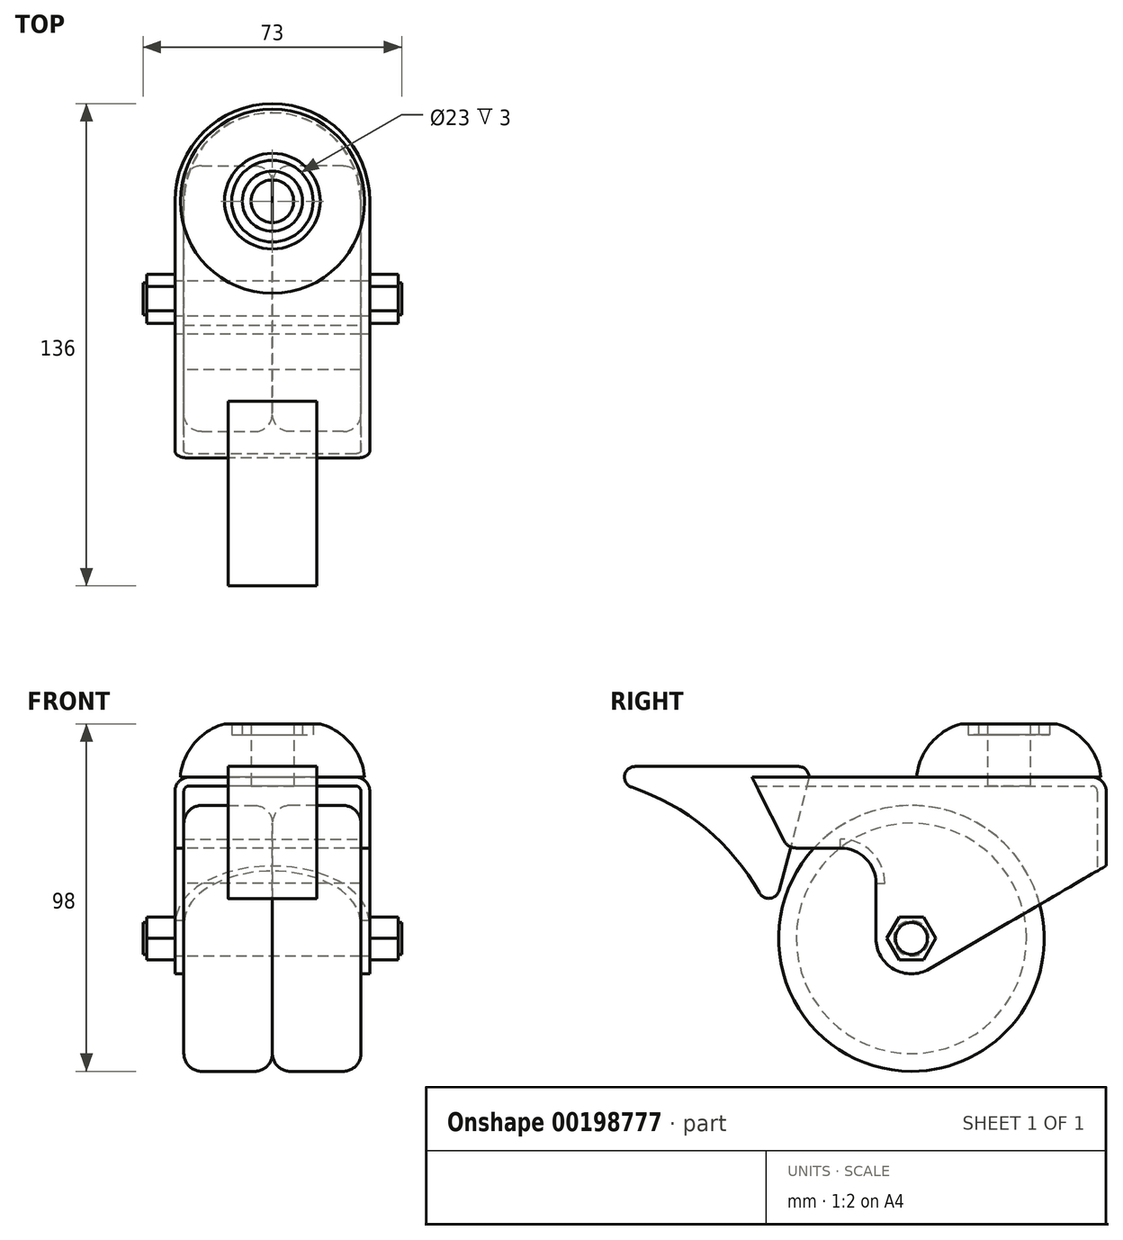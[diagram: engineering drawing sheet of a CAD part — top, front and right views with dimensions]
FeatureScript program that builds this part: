
annotation { "Feature Type Name" : "Feature", "Feature Type Description" : "" }
export const myFeature = defineFeature(function(context is Context, id is Id, definition is map)
    precondition{}
    {
        {
            var Q0;
            Q0=qCreatedBy(makeId("Right.planeOp"),FACE);
            var sketch = newSketch(context, id + "F0", { "sketchPlane" : qUnion([Q0])});
            skCircle(sketch, "E0", {"center": v(0, 0) * mm, "radius": 37.5 * mm});
            skCircle(sketch, "E1", {"center": v(0, 0) * mm, "radius": 5 * mm});
            skSolve(sketch);
        }
        {
            var Q0;
            Q0 = qSketchRegion(id + "F0", true);
            extrude(context, id + "F1", {"entities" : qUnion([Q0]), "depth" : 25 * mm});
        }
        {
            var Q0;
            Q0=makeQuery(id+"F1.opExtrude","CAP_EDGE",EDGE,{"disambiguationData":[OSD([sQuery(id+"F0.wireOp",EDGE,"E0")])],"isStart":true});
            var Q1;
            Q1=makeQuery(id+"F1.opExtrude","CAP_EDGE",EDGE,{"disambiguationData":[OSD([sQuery(id+"F0.wireOp",EDGE,"E0")])],"isStart":false});
            fillet(context, id + "F2", {"entities" : qUnion([Q0, Q1]), "radius" : 5 * mm, "tangentPropagation" : true, "allowEdgeOverflow" : false});
        }
        {
            var Q0;
            Q0=makeQuery(id+"F1.opExtrude","SWEPT_BODY",BODY,{"disambiguationData":[OSD([sQuery(id+"F0.wireOp",EDGE,"E0")])]});
            var Q1;
            Q1=qCreatedBy(makeId("Right.planeOp"),FACE);
            mirror(context, id + "F3", {"operationType" : NewBodyOperationType.ADD, "entities" : qUnion([Q0]), "mirrorPlane" : qUnion([Q1])});
        }
        {
            var Q0;
            Q0=qCreatedBy(makeId("Right.planeOp"),FACE);
            var sketch = newSketch(context, id + "F4", { "sketchPlane" : qUnion([Q0])});
            skCircle(sketch, "E2.0", {"center": v(0, 0) * mm, "radius": 5 * mm});
            skArc(sketch, "E3", {"start": v(-10, 0) * mm, "mid": v(-4.98, -8.67) * mm, "end": v(5.04, -8.64) * mm});
            skLineSegment(sketch, "E4", {"start": v(0, -37.5) * mm, "end": v(0, 45.5) * mm, "construction": true});
            skLineSegment(sketch, "E5", {"start": v(-45, 45.5) * mm, "end": v(55, 45.5) * mm});
            skLineSegment(sketch, "E6", {"start": v(-10, 0) * mm, "end": v(-10, 25.5) * mm});
            skLineSegment(sketch, "E7", {"start": v(-10, 25.5) * mm, "end": v(-35, 25.5) * mm});
            skLineSegment(sketch, "E8", {"start": v(-35, 25.5) * mm, "end": v(-45, 45.5) * mm});
            skLineSegment(sketch, "E9", {"start": v(5.04, -8.64) * mm, "end": v(55, 20.5) * mm});
            skLineSegment(sketch, "E10", {"start": v(55, 20.5) * mm, "end": v(55, 45.5) * mm});
            skSolve(sketch);
        }
        {
            var Q0;
            Q0 = qSketchRegion(id + "F4", true);
            extrude(context, id + "F5", {"entities" : qUnion([Q0]), "depth" : 55 * mm, "symmetric" : true});
        }
        {
            var Q0;
            Q0=makeQuery(id+"F5.opExtrude","CAP_EDGE",EDGE,{"disambiguationData":[OSD([sQuery(id+"F4.wireOp",EDGE,"E10")])],"isStart":false});
            var Q1;
            Q1=makeQuery(id+"F5.opExtrude","CAP_EDGE",EDGE,{"disambiguationData":[OSD([sQuery(id+"F4.wireOp",EDGE,"E10")])],"isStart":true});
            fillet(context, id + "F6", {"entities" : qUnion([Q0, Q1]), "radius" : (55 / 2) * mm, "tangentPropagation" : true, "allowEdgeOverflow" : false});
        }
        {
            var Q0;
            Q0=makeQuery(id+"F5.opExtrude","SWEPT_EDGE",EDGE,{"disambiguationData":[OSD([sQuery(id+"F4.wireOp",EDGE,"E6"),sQuery(id+"F4.wireOp",EDGE,"E7")])]});
            fillet(context, id + "F7", {"entities" : qUnion([Q0]), "radius" : 10 * mm, "tangentPropagation" : true, "allowEdgeOverflow" : false});
        }
        {
            var Q0;
            Q0=makeQuery(id+"F5.opExtrude","CAP_EDGE",EDGE,{"disambiguationData":[OSD([sQuery(id+"F4.wireOp",EDGE,"E5")])],"isStart":false});
            var Q1;
            Q1=makeQuery(id+"F5.opExtrude","SWEPT_EDGE",EDGE,{"disambiguationData":[OSD([sQuery(id+"F4.wireOp",EDGE,"E7"),sQuery(id+"F4.wireOp",EDGE,"E8")])]});
            fillet(context, id + "F8", {"entities" : qUnion([Q0, Q1]), "radius" : 4 * mm, "tangentPropagation" : true, "allowEdgeOverflow" : false});
        }
        {
            var Q0;
            Q0=makeQuery(id+"F5.opExtrude","SWEPT_FACE",FACE,{"disambiguationData":[OSD([sQuery(id+"F4.wireOp",EDGE,"E8")])]});
            var Q1;
            Q1=makeQuery(id+"F8.opFillet","BLEND_FACE",FACE,{"disambiguationData":[OSD([sQuery(id+"F4.wireOp",EDGE,"E7"),sQuery(id+"F4.wireOp",EDGE,"E8")])]});
            var Q2;
            Q2=makeQuery(id+"F5.opExtrude","SWEPT_FACE",FACE,{"disambiguationData":[OSD([sQuery(id+"F4.wireOp",EDGE,"E7")])]});
            var Q3;
            Q3=makeQuery(id+"F5.opExtrude","SWEPT_FACE",FACE,{"disambiguationData":[OSD([sQuery(id+"F4.wireOp",EDGE,"E6")])]});
            var Q4;
            Q4=makeQuery(id+"F5.opExtrude","SWEPT_FACE",FACE,{"disambiguationData":[OSD([sQuery(id+"F4.wireOp",EDGE,"E3")])]});
            var Q5;
            Q5=makeQuery(id+"F5.opExtrude","SWEPT_FACE",FACE,{"disambiguationData":[OSD([sQuery(id+"F4.wireOp",EDGE,"E2.0")])]});
            var Q6;
            Q6=makeQuery(id+"F5.opExtrude","SWEPT_FACE",FACE,{"disambiguationData":[OSD([sQuery(id+"F4.wireOp",EDGE,"E9")])]});
            shell(context, id + "F9", {"entities" : qUnion([Q0, Q1, Q2, Q3, Q4, Q5, Q6]), "thickness" : 2.5 * mm});
        }
        {
            var Q0;
            Q0=qCreatedBy(makeId("Right.planeOp"),FACE);
            var sketch = newSketch(context, id + "F10", { "sketchPlane" : qUnion([Q0])});
            skLineSegment(sketch, "E11.0", {"start": v(27.5, 45.5) * mm, "end": v(51, 45.5) * mm, "construction": true});
            skLineSegment(sketch, "E12", {"start": v(27.5, 45.5) * mm, "end": v(27.5, 60.5) * mm, "construction": true});
            skLineSegment(sketch, "E13.0", {"start": v(33.5, 45.5) * mm, "end": v(33.5, 60.5) * mm});
            skLineSegment(sketch, "E14", {"start": v(33.5, 60.5) * mm, "end": v(36, 60.5) * mm});
            skLineSegment(sketch, "E15", {"start": v(36, 60.5) * mm, "end": v(36, 57.5) * mm});
            skLineSegment(sketch, "E16", {"start": v(36, 57.5) * mm, "end": v(39, 57.5) * mm});
            skLineSegment(sketch, "E17", {"start": v(39, 57.5) * mm, "end": v(39, 60.5) * mm});
            skLineSegment(sketch, "E18", {"start": v(39, 60.5) * mm, "end": v(41, 60.5) * mm});
            skLineSegment(sketch, "E19", {"start": v(33.5, 45.5) * mm, "end": v(53.5, 45.5) * mm});
            skArc(sketch, "E20", {"start": v(53.5, 45.5) * mm, "mid": v(49.62, 54.97) * mm, "end": v(41, 60.5) * mm});
            skSolve(sketch);
        }
        {
            var Q0;
            Q0=makeQuery(id+"F10.imprint","IMPRINT",FACE,{"disambiguationData":[TD([[makeQuery(id+"F10.imprint","IMPRINT",EDGE,{"derivedFrom":sQuery(id+"F10.wireOp",EDGE,"E13.0")}),-1.0]])]});
            var Q1;
            Q1=sQuery(id+"F10.wireOp",EDGE,"E12");
            revolve(context, id + "F11", {"entities" : qUnion([Q0]), "axis" : qUnion([Q1]), "revolveType" : RevolveType.FULL});
        }
        {
            var Q0;
            {var subQ0=sQuery(id+"F4.wireOp",EDGE,"E5");Q0=makeQuery(id+"F9.opShell","OFFSET_FACE",FACE,{"disambiguationData":[OSD([subQ0]),TDD([makeQuery(id+"F5.opExtrude","SWEPT_FACE",FACE,{"disambiguationData":[OSD([subQ0])]})])]});}
            var sketch = newSketch(context, id + "F12", { "sketchPlane" : qUnion([Q0])});
            skCircle(sketch, "E21.0", {"center": v(0, -27.5) * mm, "radius": 6 * mm});
            skSolve(sketch);
        }
        {
            var Q0;
            Q0 = qSketchRegion(id + "F12", true);
            extrude(context, id + "F13", {"entities" : qUnion([Q0]), "operationType" : NewBodyOperationType.REMOVE, "oppositeDirection" : true, "depth" : 43.9 * mm});
        }
        {
            var Q0;
            Q0=makeQuery(id+"F5.opExtrude","CAP_FACE",FACE,{"disambiguationData":[OSD([sQuery(id+"F4.wireOp",EDGE,"E2.0"),sQuery(id+"F4.wireOp",EDGE,"E3"),sQuery(id+"F4.wireOp",EDGE,"E5"),sQuery(id+"F4.wireOp",EDGE,"E6"),sQuery(id+"F4.wireOp",EDGE,"E7"),sQuery(id+"F4.wireOp",EDGE,"E8"),sQuery(id+"F4.wireOp",EDGE,"E9"),sQuery(id+"F4.wireOp",EDGE,"E10")])],"isStart":false});
            var sketch = newSketch(context, id + "F14", { "sketchPlane" : qUnion([Q0])});
            skCircle(sketch, "E22.0", {"center": v(0, 0) * mm, "radius": 5 * mm, "construction": true});
            skCircle(sketch, "E23.cCircle", {"center": v(0, 0) * mm, "radius": 6 * mm, "construction": true});
            skLineSegment(sketch, "E23.0", {"start": v(-3.46, 6) * mm, "end": v(3.46, 6) * mm});
            skLineSegment(sketch, "E23.1", {"start": v(3.46, 6) * mm, "end": v(6.93, 0) * mm});
            skLineSegment(sketch, "E23.2", {"start": v(6.93, 0) * mm, "end": v(3.46, -6) * mm});
            skLineSegment(sketch, "E23.3", {"start": v(3.46, -6) * mm, "end": v(-3.46, -6) * mm});
            skLineSegment(sketch, "E23.4", {"start": v(-3.46, -6) * mm, "end": v(-6.93, 0) * mm});
            skLineSegment(sketch, "E23.5", {"start": v(-6.93, 0) * mm, "end": v(-3.46, 6) * mm});
            skPoint(sketch, "E23.0.midPoint", {"position": v(0, 6) * mm});
            skSolve(sketch);
        }
        {
            var Q0;
            Q0 = qSketchRegion(id + "F14", true);
            extrude(context, id + "F15", {"entities" : qUnion([Q0]), "depth" : 8 * mm});
        }
        {
            var Q0;
            Q0=makeQuery(id+"F15.opExtrude","CAP_FACE",FACE,{"disambiguationData":[OSD([sQuery(id+"F14.wireOp",EDGE,"E23.0"),sQuery(id+"F14.wireOp",EDGE,"E23.1"),sQuery(id+"F14.wireOp",EDGE,"E23.2"),sQuery(id+"F14.wireOp",EDGE,"E23.3"),sQuery(id+"F14.wireOp",EDGE,"E23.4"),sQuery(id+"F14.wireOp",EDGE,"E23.5")])],"isStart":false});
            var sketch = newSketch(context, id + "F16", { "sketchPlane" : qUnion([Q0])});
            skCircle(sketch, "E24", {"center": v(0, 0) * mm, "radius": 4.5 * mm});
            skSolve(sketch);
        }
        {
            var Q0;
            Q0 = qSketchRegion(id + "F16", true);
            extrude(context, id + "F17", {"entities" : qUnion([Q0]), "operationType" : NewBodyOperationType.ADD, "depth" : 1 * mm});
        }
        {
            var Q0;
            Q0=makeQuery(id+"F15.opExtrude","SWEPT_BODY",BODY,{"disambiguationData":[OSD([sQuery(id+"F14.wireOp",EDGE,"E23.0"),sQuery(id+"F14.wireOp",EDGE,"E23.1"),sQuery(id+"F14.wireOp",EDGE,"E23.2"),sQuery(id+"F14.wireOp",EDGE,"E23.3"),sQuery(id+"F14.wireOp",EDGE,"E23.4"),sQuery(id+"F14.wireOp",EDGE,"E23.5")])]});
            var Q1;
            Q1=qCreatedBy(makeId("Right.planeOp"),FACE);
            mirror(context, id + "F18", {"operationType" : NewBodyOperationType.ADD, "entities" : qUnion([Q0]), "mirrorPlane" : qUnion([Q1])});
        }
        {
            var Q0;
            Q0=qCreatedBy(makeId("Right.planeOp"),FACE);
            var sketch = newSketch(context, id + "F19", { "sketchPlane" : qUnion([Q0])});
            skLineSegment(sketch, "E25", {"start": v(-78, 48.5) * mm, "end": v(-31.9, 48.5) * mm});
            skLineSegment(sketch, "E26", {"start": v(-29.01, 44.72) * mm, "end": v(-37.38, 13.5) * mm});
            skLineSegment(sketch, "E27", {"start": v(-37.38, 13.5) * mm, "end": v(-78, 48.5) * mm, "construction": true});
            skArc(sketch, "E28", {"start": v(-78, 48.5) * mm, "mid": v(-80.96, 45.98) * mm, "end": v(-78.95, 42.66) * mm});
            skLineSegment(sketch, "E29.0", {"start": v(-30.9, 49.28) * mm, "end": v(-43.27, 3.09) * mm, "construction": true});
            skArc(sketch, "E30", {"start": v(-42.9, 12.8) * mm, "mid": v(-39.9, 11.3) * mm, "end": v(-37.38, 13.5) * mm});
            skArc(sketch, "E31", {"start": v(-42.9, 12.8) * mm, "mid": v(-58.14, 31.1) * mm, "end": v(-78.95, 42.66) * mm});
            skPoint(sketch, "E32.visualSharp", {"position": v(-28, 48.5) * mm});
            skArc(sketch, "E32.filletArc", {"start": v(-29.01, 44.72) * mm, "mid": v(-29.53, 47.33) * mm, "end": v(-31.9, 48.5) * mm});
            skLineSegment(sketch, "E33", {"start": v(-37.38, 13.5) * mm, "end": v(-37.38, 13.5) * mm});
            skSolve(sketch);
        }
        {
            var Q0;
            Q0 = qSketchRegion(id + "F19", true);
            extrude(context, id + "F20", {"entities" : qUnion([Q0]), "depth" : 25 * mm, "symmetric" : true});
        }
    });
